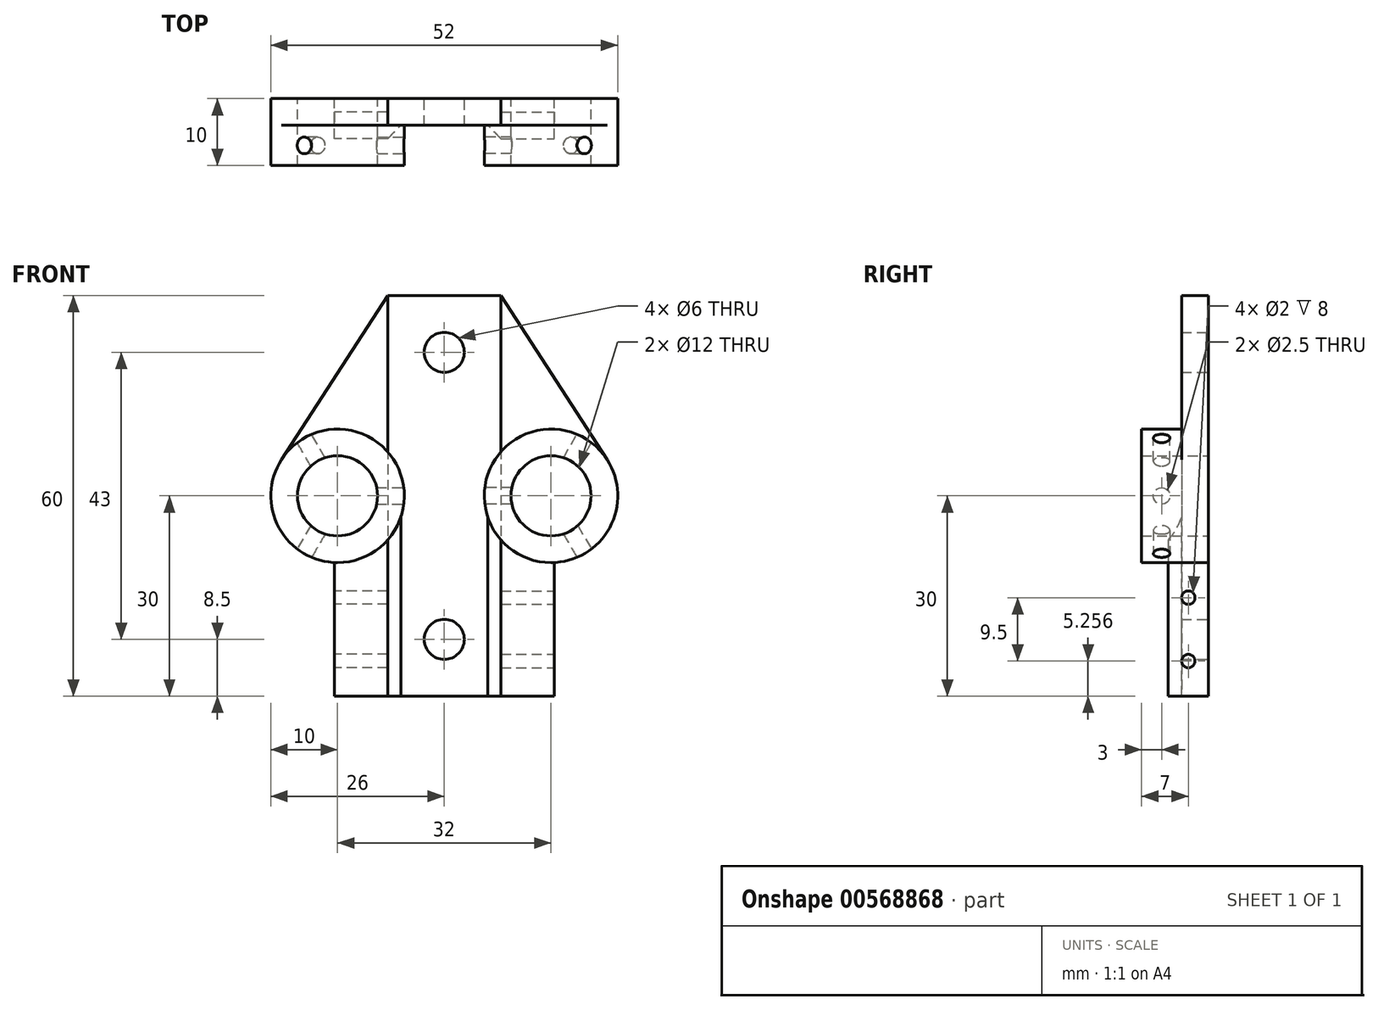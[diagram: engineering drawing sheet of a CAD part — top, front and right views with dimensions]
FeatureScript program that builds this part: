
annotation { "Feature Type Name" : "Feature", "Feature Type Description" : "" }
export const myFeature = defineFeature(function(context is Context, id is Id, definition is map)
    precondition{}
    {
        {
            var Q0;
            Q0=qCreatedBy(makeId("Front.planeOp"),FACE);
            var sketch = newSketch(context, id + "F0", { "sketchPlane" : qUnion([Q0])});
            skLineSegment(sketch, "E0.bottom", {"start": v(-8.5, 30) * mm, "end": v(8.5, 30) * mm});
            skLineSegment(sketch, "E0.top", {"start": v(-8.5, -30) * mm, "end": v(8.5, -30) * mm});
            skLineSegment(sketch, "E0.left", {"start": v(-8.5, 30) * mm, "end": v(-8.5, -30) * mm});
            skCircle(sketch, "E1", {"center": v(16, 0) * mm, "radius": 6 * mm});
            skCircle(sketch, "E2", {"center": v(16, 0) * mm, "radius": 9.5 * mm, "construction": true});
            skCircle(sketch, "E3", {"center": v(16, 0) * mm, "radius": 12.5 * mm, "construction": true});
            skCircle(sketch, "E4", {"center": v(16, 0) * mm, "radius": 5 * mm, "construction": true});
            skLineSegment(sketch, "E5", {"start": v(24.4, -5.43) * mm, "end": v(8.5, -30) * mm});
            skLineSegment(sketch, "E6", {"start": v(24.4, 5.43) * mm, "end": v(8.5, 30) * mm});
            skCircle(sketch, "E7.converted", {"center": v(16, 0) * mm, "radius": 10 * mm});
            skCircle(sketch, "E8", {"center": v(0, 21.5) * mm, "radius": 3 * mm});
            skCircle(sketch, "E9", {"center": v(0, -21.5) * mm, "radius": 3 * mm});
            skLineSegment(sketch, "E10", {"start": v(0, 30) * mm, "end": v(0, 21.5) * mm, "construction": true});
            skLineSegment(sketch, "E11", {"start": v(0, 21.5) * mm, "end": v(-8.5, 21.5) * mm, "construction": true});
            skLineSegment(sketch, "E12", {"start": v(0, -21.5) * mm, "end": v(-8.5, -21.5) * mm, "construction": true});
            skLineSegment(sketch, "E13", {"start": v(0, -21.5) * mm, "end": v(0, -30) * mm, "construction": true});
            skLineSegment(sketch, "E14", {"start": v(10, 41.16) * mm, "end": v(10, -39.22) * mm, "construction": true});
            skLineSegment(sketch, "E15", {"start": v(-10, 39.22) * mm, "end": v(-10, -37.67) * mm, "construction": true});
            skSolve(sketch);
        }
        {
            var Q0;
            Q0 = qSketchRegion(id + "F0", true);
            extrude(context, id + "F1", {"entities" : qUnion([Q0]), "depth" : 4 * mm, "offsetDistance" : 25 * mm});
        }
        {
            var Q0;
            Q0=makeQuery(id+"F0.imprint","IMPRINT",FACE,{"disambiguationData":[TD([[makeQuery(id+"F0.imprint","IMPRINT",EDGE,{"derivedFrom":sQuery(id+"F0.wireOp",EDGE,"E1")}),-1.0]])]});
            extrude(context, id + "F2", {"entities" : qUnion([Q0]), "operationType" : NewBodyOperationType.ADD, "depth" : 10 * mm, "offsetDistance" : 25 * mm});
        }
        {
            var Q0;
            {var subQ0=sQuery(id+"F0.wireOp",EDGE,"E0.left");var subQ1=sQuery(id+"F0.wireOp",EDGE,"E0.top");var subQ2=sQuery(id+"F0.wireOp",EDGE,"E5");var subQ3=sQuery(id+"F0.wireOp",EDGE,"E0.bottom");var subQ4=sQuery(id+"F0.wireOp",EDGE,"E6");var subQ5=sQuery(id+"F0.wireOp",EDGE,"E7.converted");var subQ6=sQuery(id+"F0.wireOp",EDGE,"E8");var subQ7=sQuery(id+"F0.wireOp",EDGE,"E9");Q0=makeQuery(id+"F2.boolean.opBoolean","SPLIT",FACE,{"disambiguationData":[TD([makeQuery(id+"F1.opExtrude","SWEPT_FACE",FACE,{"disambiguationData":[OSD([subQ3])]})])],"derivedFrom":makeQuery(id+"F1.opExtrude","CAP_FACE",FACE,{"disambiguationData":[OSD([subQ3,subQ1,subQ0,subQ2,subQ4,subQ5,subQ6,subQ7])],"isStart":false})});}
            cPlane(context, id + "F3", {"entities" : qUnion([Q0]), "cplaneType" : CPlaneType.OFFSET, "offset" : 3 * mm, "width" : 150 * mm, "height" : 150 * mm});
        }
        {
            var Q0;
            Q0=qCreatedBy(id+"F3.planeOp",FACE);
            var sketch = newSketch(context, id + "F4", { "sketchPlane" : qUnion([Q0])});
            skCircle(sketch, "E16.0", {"center": v(16, 0) * mm, "radius": 6 * mm, "construction": true});
            skCircle(sketch, "E17.0", {"center": v(16, 0) * mm, "radius": 10 * mm, "construction": true});
            skLineSegment(sketch, "E18", {"start": v(16, 0) * mm, "end": v(2.56, 0) * mm, "construction": true});
            skLineSegment(sketch, "E19.bottom", {"start": v(10.13, -1.25) * mm, "end": v(6, -1.25) * mm});
            skLineSegment(sketch, "E19.top", {"start": v(10.13, 0) * mm, "end": v(6, 0) * mm});
            skLineSegment(sketch, "E19.left", {"start": v(10.13, -1.25) * mm, "end": v(10.13, 0) * mm});
            skLineSegment(sketch, "E19.right", {"start": v(6, -1.25) * mm, "end": v(6, 0) * mm});
            skLineSegment(sketch, "E20.1.0", {"start": v(16, 0) * mm, "end": v(22.72, -11.64) * mm, "construction": true});
            skLineSegment(sketch, "E20.1.1", {"start": v(20.02, -4.46) * mm, "end": v(22.08, -8.04) * mm});
            skLineSegment(sketch, "E20.1.2", {"start": v(20.02, -4.46) * mm, "end": v(18.93, -5.08) * mm});
            skLineSegment(sketch, "E20.1.3", {"start": v(18.93, -5.08) * mm, "end": v(21, -8.66) * mm});
            skLineSegment(sketch, "E20.1.4", {"start": v(22.08, -8.04) * mm, "end": v(21, -8.66) * mm});
            skLineSegment(sketch, "E20.2.0", {"start": v(16, 0) * mm, "end": v(22.72, 11.64) * mm, "construction": true});
            skLineSegment(sketch, "E20.2.1", {"start": v(17.85, 5.7) * mm, "end": v(19.92, 9.29) * mm});
            skLineSegment(sketch, "E20.2.2", {"start": v(17.85, 5.7) * mm, "end": v(18.93, 5.08) * mm});
            skLineSegment(sketch, "E20.2.3", {"start": v(18.93, 5.08) * mm, "end": v(21, 8.66) * mm});
            skLineSegment(sketch, "E20.2.4", {"start": v(19.92, 9.29) * mm, "end": v(21, 8.66) * mm});
            skSolve(sketch);
        }
        {
            var Q0;
            Q0=makeQuery(id+"F4.imprint","IMPRINT",FACE,{"disambiguationData":[TD([[makeQuery(id+"F4.imprint","IMPRINT",EDGE,{"derivedFrom":sQuery(id+"F4.wireOp",EDGE,"E19.bottom")}),-1.0]])]});
            var Q1;
            Q1=sQuery(id+"F4.wireOp",EDGE,"E18");
            revolve(context, id + "F5", {"operationType" : NewBodyOperationType.REMOVE, "entities" : qUnion([Q0]), "axis" : qUnion([Q1]), "revolveType" : RevolveType.FULL, "oppositeDirection" : true});
        }
        {
            var Q0;
            Q0=makeQuery(id+"F4.imprint","IMPRINT",FACE,{"disambiguationData":[TD([[makeQuery(id+"F4.imprint","IMPRINT",EDGE,{"derivedFrom":sQuery(id+"F4.wireOp",EDGE,"E20.1.1")}),-1.0]])]});
            var Q1;
            Q1=sQuery(id+"F4.wireOp",EDGE,"E20.1.0");
            revolve(context, id + "F6", {"operationType" : NewBodyOperationType.REMOVE, "entities" : qUnion([Q0]), "axis" : qUnion([Q1]), "revolveType" : RevolveType.FULL, "oppositeDirection" : true});
        }
        {
            var Q0;
            Q0=makeQuery(id+"F4.imprint","IMPRINT",FACE,{"disambiguationData":[TD([[makeQuery(id+"F4.imprint","IMPRINT",EDGE,{"derivedFrom":sQuery(id+"F4.wireOp",EDGE,"E20.2.1")}),-1.0]])]});
            var Q1;
            Q1=sQuery(id+"F4.wireOp",EDGE,"E20.2.0");
            revolve(context, id + "F7", {"operationType" : NewBodyOperationType.REMOVE, "entities" : qUnion([Q0]), "axis" : qUnion([Q1]), "revolveType" : RevolveType.FULL, "oppositeDirection" : true});
        }
        {
            var Q0;
            Q0=qCreatedBy(makeId("Front.planeOp"),FACE);
            var sketch = newSketch(context, id + "F8", { "sketchPlane" : qUnion([Q0])});
            skLineSegment(sketch, "E21.0", {"start": v(-8.5, 30) * mm, "end": v(-8.5, -30) * mm, "construction": true});
            skCircle(sketch, "E21.2", {"center": v(16, 0) * mm, "radius": 6 * mm, "construction": true});
            skLineSegment(sketch, "E21.3", {"start": v(24.4, 5.43) * mm, "end": v(8.5, 30) * mm, "construction": true});
            skLineSegment(sketch, "E21.4", {"start": v(24.4, -5.43) * mm, "end": v(8.5, -30) * mm, "construction": true});
            skLineSegment(sketch, "E21.5", {"start": v(-8.5, -30) * mm, "end": v(8.5, -30) * mm, "construction": true});
            skLineSegment(sketch, "E21.6", {"start": v(-8.5, 30) * mm, "end": v(8.5, 30) * mm, "construction": true});
            skCircle(sketch, "E21.7", {"center": v(0, 21.5) * mm, "radius": 3 * mm, "construction": true});
            skCircle(sketch, "E21.8", {"center": v(0, -21.5) * mm, "radius": 3 * mm, "construction": true});
            skLineSegment(sketch, "E22", {"start": v(8.5, -30) * mm, "end": v(16.5, -30) * mm});
            skLineSegment(sketch, "E23", {"start": v(16.5, -30) * mm, "end": v(16.5, -9.99) * mm});
            skLineSegment(sketch, "E24", {"start": v(8.5, -6.61) * mm, "end": v(8.5, -30) * mm});
            skArc(sketch, "E25", {"start": v(16.5, -9.99) * mm, "mid": v(21, -8.66) * mm, "end": v(24.4, -5.43) * mm});
            skArc(sketch, "E26", {"start": v(24.4, -5.43) * mm, "mid": v(15.26, 9.97) * mm, "end": v(8.5, -6.61) * mm, "construction": true});
            skArc(sketch, "E27", {"start": v(8.5, -6.61) * mm, "mid": v(12.11, -9.21) * mm, "end": v(16.5, -9.99) * mm});
            skLineSegment(sketch, "E28", {"start": v(24.4, -5.43) * mm, "end": v(24.4, -30) * mm});
            skLineSegment(sketch, "E29", {"start": v(24.4, -30) * mm, "end": v(16.5, -30) * mm});
            skSolve(sketch);
        }
        {
            var Q0;
            Q0=makeQuery(id+"F8.imprint","IMPRINT",FACE,{"disambiguationData":[TD([[makeQuery(id+"F8.imprint","IMPRINT",EDGE,{"derivedFrom":sQuery(id+"F8.wireOp",EDGE,"E22")}),1.0]])]});
            extrude(context, id + "F9", {"entities" : qUnion([Q0]), "operationType" : NewBodyOperationType.ADD, "depth" : 6 * mm, "offsetDistance" : 25 * mm});
        }
        {
            var Q0;
            {var subQ0=sQuery(id+"F0.wireOp",EDGE,"E0.left");var subQ1=sQuery(id+"F0.wireOp",EDGE,"E0.top");var subQ2=sQuery(id+"F0.wireOp",EDGE,"E5");var subQ3=sQuery(id+"F0.wireOp",EDGE,"E0.bottom");var subQ4=sQuery(id+"F0.wireOp",EDGE,"E6");var subQ5=sQuery(id+"F0.wireOp",EDGE,"E7.converted");var subQ6=sQuery(id+"F0.wireOp",EDGE,"E8");var subQ7=sQuery(id+"F0.wireOp",EDGE,"E9");Q0=makeQuery(id+"F9.boolean.opBoolean","INTERSECT",EDGE,{"derivedFrom":[makeQuery(id+"F2.boolean.opBoolean","SPLIT",FACE,{"disambiguationData":[TD([makeQuery(id+"F1.opExtrude","SWEPT_FACE",FACE,{"disambiguationData":[OSD([subQ3])]})])],"derivedFrom":makeQuery(id+"F1.opExtrude","CAP_FACE",FACE,{"disambiguationData":[OSD([subQ3,subQ1,subQ0,subQ2,subQ4,subQ5,subQ6,subQ7])],"isStart":false})}),makeQuery(id+"F9.opExtrude","SWEPT_FACE",FACE,{"disambiguationData":[OSD([sQuery(id+"F8.wireOp",EDGE,"E24")])]})]});}
            chamfer(context, id + "F10", {"entities" : qUnion([Q0]), "width" : 2 * mm, "tangentPropagation" : true});
        }
        {
            var Q0;
            Q0=makeQuery(id+"F8.imprint","IMPRINT",FACE,{"disambiguationData":[TD([[makeQuery(id+"F8.imprint","IMPRINT",EDGE,{"derivedFrom":sQuery(id+"F8.wireOp",EDGE,"E23")}),-1.0]])]});
            extrude(context, id + "F11", {"entities" : qUnion([Q0]), "operationType" : NewBodyOperationType.REMOVE, "depth" : 25 * mm, "offsetDistance" : 25 * mm});
        }
        {
            var Q0;
            Q0=makeQuery(id+"F9.opExtrude","SWEPT_FACE",FACE,{"disambiguationData":[OSD([sQuery(id+"F8.wireOp",EDGE,"E23")])]});
            var sketch = newSketch(context, id + "F12", { "sketchPlane" : qUnion([Q0])});
            skLineSegment(sketch, "E30.0", {"start": v(-6, -9.99) * mm, "end": v(0, -9.99) * mm, "construction": true});
            skLineSegment(sketch, "E30.1", {"start": v(0, -30) * mm, "end": v(0, -9.99) * mm, "construction": true});
            skLineSegment(sketch, "E30.2", {"start": v(-6, -30) * mm, "end": v(0, -30) * mm, "construction": true});
            skLineSegment(sketch, "E30.3", {"start": v(-6, -30) * mm, "end": v(-6, -9.99) * mm, "construction": true});
            skCircle(sketch, "E31", {"center": v(-3, -15.24) * mm, "radius": 1 * mm});
            skCircle(sketch, "E32", {"center": v(-3, -24.74) * mm, "radius": 1 * mm});
            skLineSegment(sketch, "E33", {"start": v(-3, -9.99) * mm, "end": v(-3, -15.24) * mm, "construction": true});
            skLineSegment(sketch, "E34", {"start": v(-3, -24.74) * mm, "end": v(-3, -30) * mm, "construction": true});
            skSolve(sketch);
        }
        {
            var Q0;
            Q0 = qSketchRegion(id + "F12", true);
            extrude(context, id + "F13", {"entities" : qUnion([Q0]), "operationType" : NewBodyOperationType.REMOVE, "oppositeDirection" : true, "depth" : 8 * mm, "offsetDistance" : 25 * mm});
        }
        {
            var Q0;
            Q0=makeQuery(id+"F1.opExtrude","SWEPT_BODY",BODY,{"disambiguationData":[OSD([sQuery(id+"F0.wireOp",EDGE,"E0.bottom"),sQuery(id+"F0.wireOp",EDGE,"E0.top"),sQuery(id+"F0.wireOp",EDGE,"E0.left"),sQuery(id+"F0.wireOp",EDGE,"E5"),sQuery(id+"F0.wireOp",EDGE,"E6"),sQuery(id+"F0.wireOp",EDGE,"E7.converted"),sQuery(id+"F0.wireOp",EDGE,"E8"),sQuery(id+"F0.wireOp",EDGE,"E9")])]});
            var Q1;
            Q1=qCreatedBy(makeId("Right.planeOp"),FACE);
            mirror(context, id + "F14", {"entities" : qUnion([Q0]), "mirrorPlane" : qUnion([Q1])});
        }
    });
